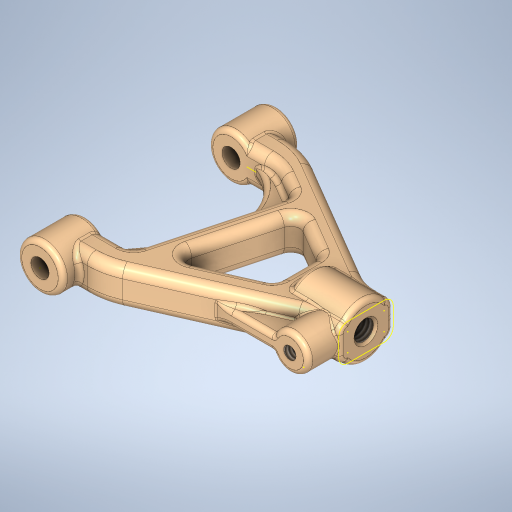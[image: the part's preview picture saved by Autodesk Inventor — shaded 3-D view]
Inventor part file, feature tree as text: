
AUTODESK INVENTOR PART (.ipt)
format: ipt  version: 2024 (Build 280153000, 153)  size: 1,249,280 bytes
history: native  units: in
note: dims shown in document units (in); Inventor stores cm internally (conversion verified against a paired STEP export)
features: fillet x19, sketch x9, extrude x6, projected_geometry x4, rib x3, plane x2, hole x2, chamfer x1
ambient origin geometry x8: Origin, YZ Plane, XZ Plane, XY Plane, X Axis, Y Axis, Z Axis, Center Point
bodies: Solid1 (feature_tree)
feature tree (46):
  extrude  "Extrusion1"  Depth=0.315in TaperAngle=0.0deg
  plane  "Work Plane1"
  extrude  "Extrusion2"  Depth=0.315in TaperAngle=0.0deg
  extrude  "Extrusion3"  Depth=0.375in
  fillet  "Fillet1"  Radius=0.5in
  fillet  "Fillet2"  Radius=1.5in
  fillet  "Fillet3"  Radius=0.188in
  fillet  "Fillet4"  Radius=0.315in
  fillet  "Fillet5"  Radius=0.2in
  fillet  "Fillet6"  Radius=0.2in
  fillet  "Fillet7"  [1 undecoded]
  rib  "Rib1"
  fillet  "Fillet8"  Radius=0.15in
  rib  "Rib2"
  fillet  "Fillet9"  Radius=0.25in
  sketch  "Sketch13"  dims[d6=0.742in d7=0.375in d8=0.5in d9=1.5in d10=0.188in d11=0.315in d12=0.2in d13=0.2in d14=105.0deg d15=0.15in d16=0.25in d17=0.0in]
  extrude  "Extrusion4"  Depth=0.5in
  fillet  "Fillet10"  Radius=0.0625in
  fillet  "Fillet11"  Radius=0.315in
  fillet  "Fillet12"  Radius=0.0625in
  fillet  "Fillet13"  Radius=0.0625in
  fillet  "Fillet14"  Radius=0.032in
  extrude  "Extrusion5"  Depth=0.357in
  plane  "Work Plane2"
  extrude  "Extrusion6"  Depth=0.1in
  fillet  "Fillet15"  Radius=0.032in
  rib  "Rib3"
  fillet  "Fillet16"  Radius=0.125in
  fillet  "Fillet17"  Radius=0.188in
  fillet  "Fillet18"  Radius=0.375in
  hole  "Hole1"  [1 undecoded]
  fillet  "Fillet19"  Radius=0.032in
  hole  "Hole2"  [1 undecoded]
  chamfer  "Chamfer1"  Distance=0.032in
  sketch  "Sketch4"  dims[d0=0.315in d1=0.315in d2=0.0in]
  projected_geometry  "Projected Loop1"
  projected_geometry  "Projected Loop2"
  projected_geometry  "Projected Loop3"
  sketch  "Sketch12"  dims[d3=1.0in d4=0.315in d5=0.0in]
  sketch  "Sketch14"  dims[d18=0.315in d19=0.5in d20=0.0625in d21=0.315in d22=0.0625in d23=0.0625in d24=0.032in]
  sketch  "Sketch15"  dims[d25=0.1in]
  sketch  "Sketch16"  dims[d26=0.1in d27=0.0in d28=0.0in d29=0.1in d30=0.1in d31=0.357in]
  sketch  "Sketch17"  dims[d32=0.032in d37=0.1in]
  sketch  "Sketch18"  dims[d38=0.1in d39=0.0in d40=0.0in d41=0.1in d42=0.1in d43=0.032in d45=0.125in d46=0.188in d47=0.375in]
  sketch  "Sketch19"  dims[d48=0.3875in d49=0.0in d50=0.032in d51=0.032in d52=0.032in d53=0.032in d54=0.032in d55=0.125in d56=100.0in d57=0.0in d58=0.2in d59=0.25in d60=0.135in d61=100.0in d62=0.0in d63=0.015in d64=0.1in d65=0.1in d66=0.0in d67=0.0in d68=0.1in d69=0.1in d70=0.014in d71=0.032in d72=0.032in d73=0.0849in d74=0.25in d75=0.375in d76=0.25in d77=0.5635in d78=0.25in d79=0.8108in d80=0.014in d81=0.134in d82=0.328in d83=0.375in d84=0.25in d85=0.5635in d86=0.375in d87=0.8108in d88=0.015in d89=0.125in d90=45.0deg]
  projected_geometry  "Project Cut Edges1"
note: 3 required parameter values undecoded (feature->parameter linkage not recoverable at this tier; creation-order binding heuristic only, values carry confidence <= 0.55)
